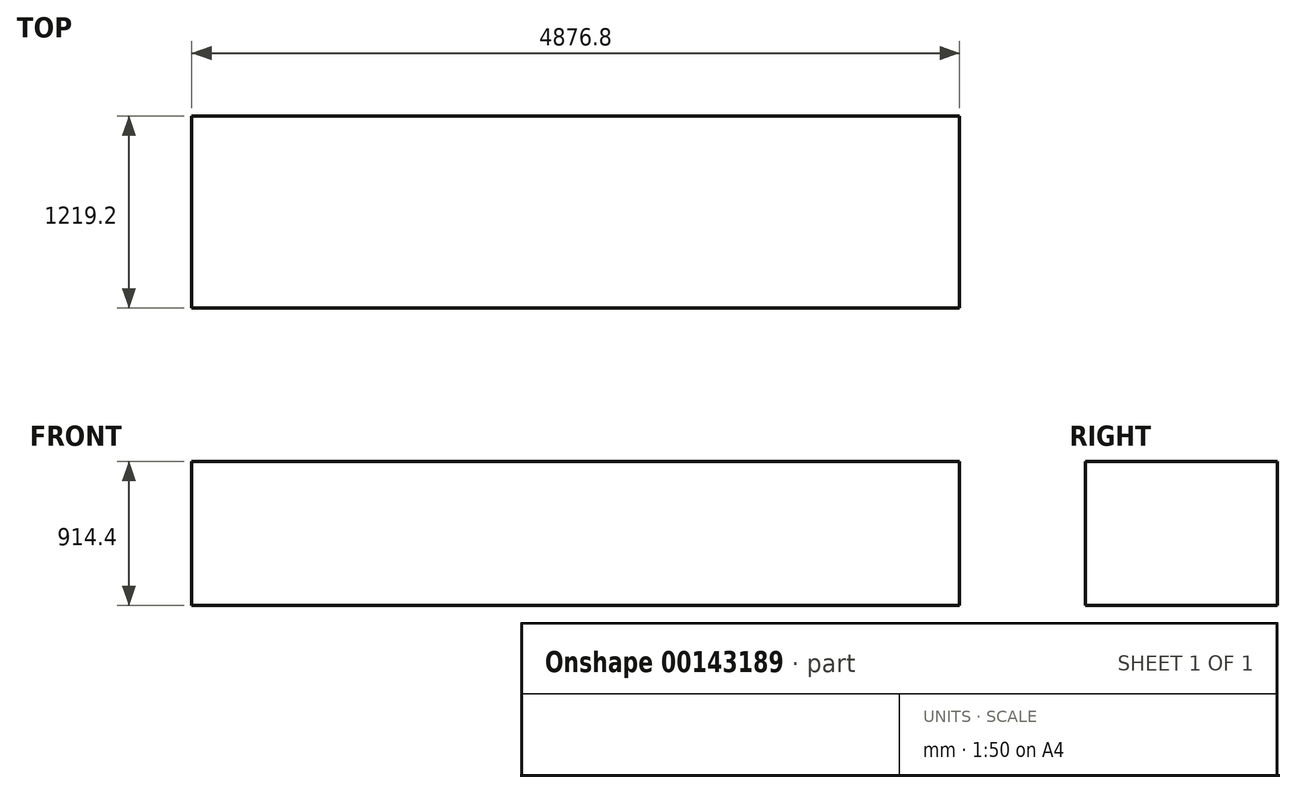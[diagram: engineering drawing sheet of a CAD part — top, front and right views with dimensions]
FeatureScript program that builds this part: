
annotation { "Feature Type Name" : "Feature", "Feature Type Description" : "" }
export const myFeature = defineFeature(function(context is Context, id is Id, definition is map)
    precondition{}
    {
        {
            var Q0;
            Q0=qCreatedBy(makeId("Top.planeOp"),FACE);
            var sketch = newSketch(context, id + "F0", { "sketchPlane" : qUnion([Q0])});
            skLineSegment(sketch, "E0.bottom", {"start": v(-1810.47, -596.84) * mm, "end": v(3066.33, -596.84) * mm});
            skLineSegment(sketch, "E0.top", {"start": v(-1810.47, 622.36) * mm, "end": v(3066.33, 622.36) * mm});
            skLineSegment(sketch, "E0.left", {"start": v(-1810.47, -596.84) * mm, "end": v(-1810.47, 622.36) * mm});
            skLineSegment(sketch, "E0.right", {"start": v(3066.33, -596.84) * mm, "end": v(3066.33, 622.36) * mm});
            skSolve(sketch);
        }
        {
            var Q0;
            Q0 = qSketchRegion(id + "F0", true);
            extrude(context, id + "F1", {"entities" : qUnion([Q0]), "oppositeDirection" : true, "depth" : 914.4 * mm});
        }
    });
